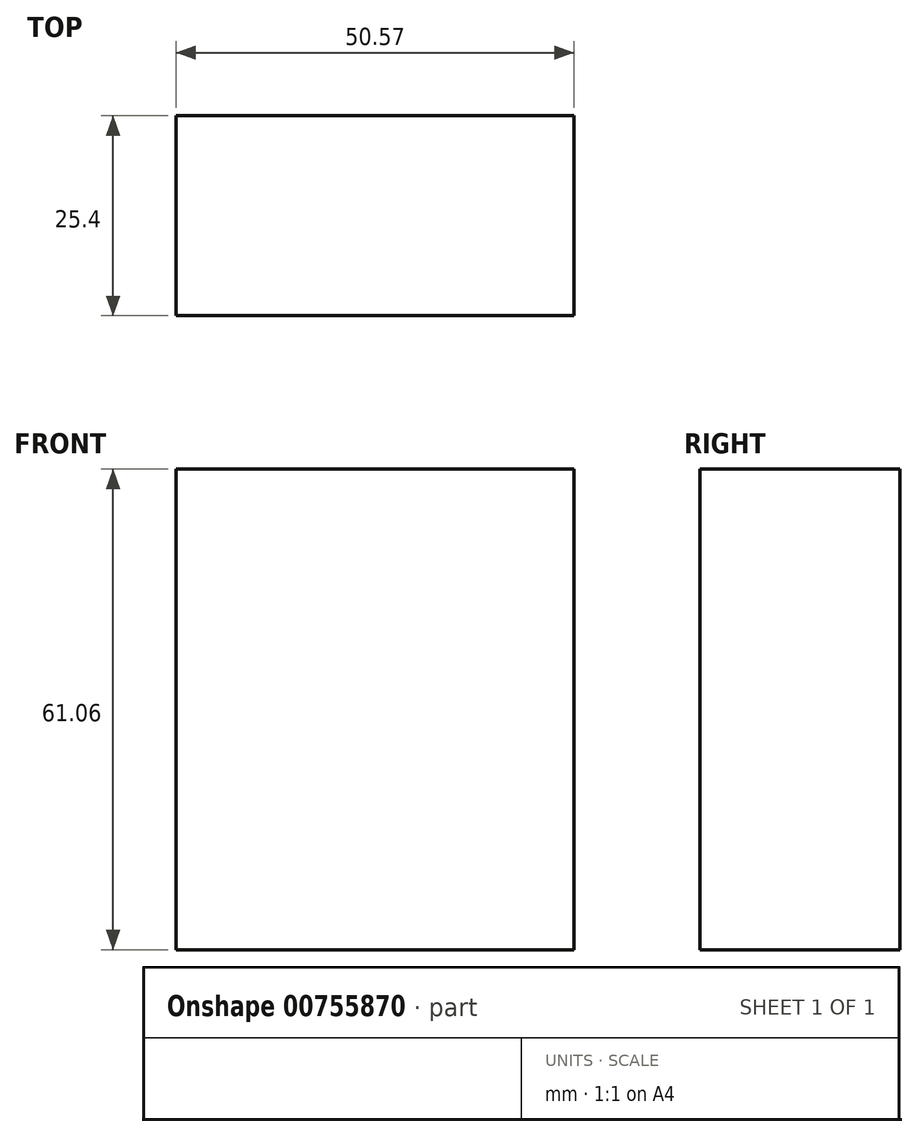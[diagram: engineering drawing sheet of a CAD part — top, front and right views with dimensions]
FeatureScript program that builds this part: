
annotation { "Feature Type Name" : "Feature", "Feature Type Description" : "" }
export const myFeature = defineFeature(function(context is Context, id is Id, definition is map)
    precondition{}
    {
        {
            var Q0;
            Q0=qCreatedBy(makeId("Front.planeOp"),FACE);
            var sketch = newSketch(context, id + "F0", { "sketchPlane" : qUnion([Q0])});
            skLineSegment(sketch, "E0.bottom", {"start": v(0, 0) * mm, "end": v(0, 0) * mm});
            skLineSegment(sketch, "E0.top", {"start": v(0, -9.44) * mm, "end": v(0, -9.44) * mm});
            skLineSegment(sketch, "E0.left", {"start": v(0, 0) * mm, "end": v(0, -9.44) * mm});
            skLineSegment(sketch, "E0.right", {"start": v(0, 0) * mm, "end": v(0, -9.44) * mm});
            skLineSegment(sketch, "E1.bottom", {"start": v(50.57, 61.06) * mm, "end": v(0, 61.06) * mm});
            skLineSegment(sketch, "E1.top", {"start": v(50.57, 0) * mm, "end": v(0, 0) * mm});
            skLineSegment(sketch, "E1.left", {"start": v(50.57, 61.06) * mm, "end": v(50.57, 0) * mm});
            skLineSegment(sketch, "E1.right", {"start": v(0, 61.06) * mm, "end": v(0, 0) * mm});
            skSolve(sketch);
        }
        {
            var Q0;
            Q0=makeQuery(id+"F0.imprint","IMPRINT",FACE,{"disambiguationData":[TD([[makeQuery(id+"F0.imprint","IMPRINT",EDGE,{"derivedFrom":sQuery(id+"F0.wireOp",EDGE,"E1.bottom")}),1.0]])]});
            extrude(context, id + "F1", {"entities" : qUnion([Q0]), "depth" : 25.4 * mm, "offsetDistance" : 25.4 * mm});
        }
    });
